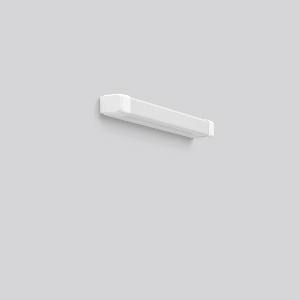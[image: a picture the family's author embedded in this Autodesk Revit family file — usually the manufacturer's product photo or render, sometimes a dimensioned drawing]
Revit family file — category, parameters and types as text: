
# Revit family: baleva_451215_002_2_2ab9
name_source: partatom
category: Lighting Fixtures
units: mm (PartAtom-declared; Revit-internal decimal feet)

## family parameters
Cut with Voids When Loaded = No
Host = Face
Light Source = No
Part Type = Normal
Room Calculation Point = No
Round Connector Dimension = Use Diameter
Shared = No

## types (1)
- MultiColor 830 (1 x LED Modul 830, 950 lm, 3000)
    Apparent Load = 9 VA
    CIE Flux Codes = 40 69 88 82 100
    Color Rendering = 80
    Color Temperature = 3000
    Default Elevation = 1800 mm
    Description = Series: BALEVA
Linear luminaire with timeless functional design. Ideal for sanitary areas, corridors, waiting areas, nursing homes, patient rooms. Body and end caps made of white plastic. Diffuser made of plastic (polycarbonate), opal, shockproof. Homogeneous and smooth light distribution. MultiColour: With rear switching element, variable colour temperature 3000  K or 4000  K. Factory setting is 4000 K. Diffuser can be assembled without the use of tools. Quick and easy to install. Can be installed horizontally and vertically. 2 central cable inlets for looping the cable. Converter integrated and encapsulated. 
Colour: white
Length: 500 mm
Width: 46 mm
Height: 60 mm
Lamp: LED
Socket: without socket
Colour temperature: 3000K, 4000K
Colour rendering index (CRI): 80
System power: 9 W
Rated luminous flux: 950 lm
Luminous efficiency: 106 lm/W
System power 2: 9 W
Rated luminous flux 2: 1000 lm
Luminous efficiency 2: 111 lm/W
Control gear: Regulated power supply
Protection class: II
Type of protection: IP 40
    Height = 60 mm  [stored 0.19685 ft]
    Lamp = 1 x LED Modul 830
    Lamp Light Flux = 950 lm
    Lamp count = 1
    Length = 500 mm
    Lifetime = 50000 h
    Luminous efficacy = 106 lm/W
    Manufacturer = RZB
    ModVariant = No
    Model = 451215.002.2
    Mounting Place = Wall, Ceiling
    Mounting Type = Surface mounted
    Number of Poles = 1
    OnlyDefault = Yes
    Power Factor = 1
    Product Name = BALEVA
    Product group = Surface mounted ceiling and wall luminaires
    ProductGroupID = 305
    Protection Class = Protection class II
    Protection Degree = IP 40
    RLX_Detail_Level = 1
    RLX_Emergency_Light_Flux = 0 lm
    RLX_Emergency_Type = 0
    RLX_Emergency_Type_DB = No
    RlxData = <blob elided: 27021 chars, md5=c9e555e5>
    Socket = socket
    Standby Power = 0 W
    System Light Flux = 950 lm
    System Power = 9 W
    Type Comments = MultiColor 830
    Type Image = 451215.002.jpg
    URL = http://relux.com
    VarID = multicolor_830
    Voltage = 230 V
    Voltage Range = 220-240 V
    Weight = 0.00 kg
    Width = 46 mm

note: [stored X ft] marks values corroborated as IEEE doubles in the binary element streams (Revit-internal decimal feet)

## geometry (parser evidence)
native form markers: Blend x4, Sweep x14
no freeform markers — native parametric forms only
